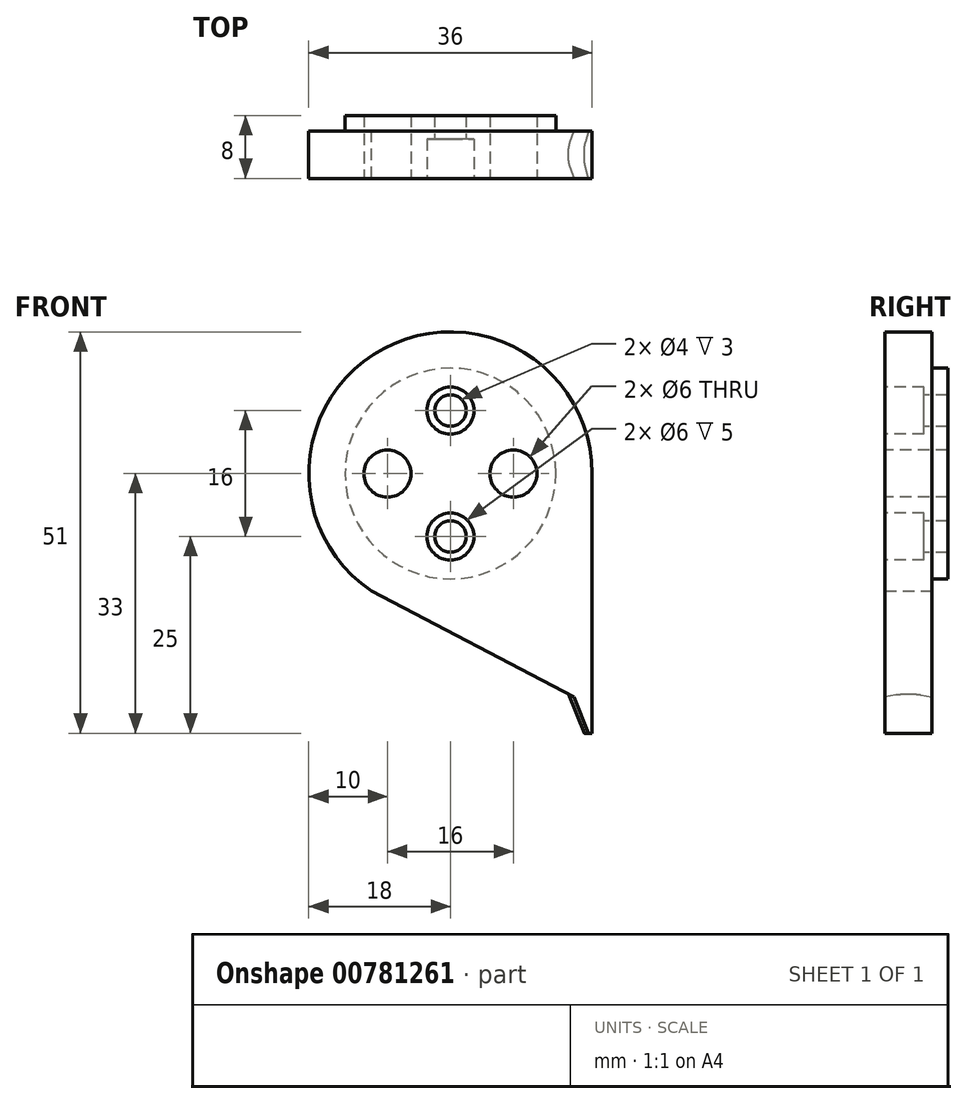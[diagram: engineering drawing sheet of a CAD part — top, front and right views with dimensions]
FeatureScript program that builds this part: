
annotation { "Feature Type Name" : "Feature", "Feature Type Description" : "" }
export const myFeature = defineFeature(function(context is Context, id is Id, definition is map)
    precondition{}
    {
        {
            var Q0;
            Q0=qCreatedBy(makeId("Front.planeOp"),FACE);
            var sketch = newSketch(context, id + "F0", { "sketchPlane" : qUnion([Q0])});
            skCircle(sketch, "E0", {"center": v(0, 0) * mm, "radius": 18 * mm});
            skLineSegment(sketch, "E1", {"start": v(18, 0) * mm, "end": v(18, -33) * mm});
            skLineSegment(sketch, "E2", {"start": v(18, -33) * mm, "end": v(15, -33) * mm});
            skLineSegment(sketch, "E3", {"start": v(15, -33) * mm, "end": v(15, -28) * mm});
            skLineSegment(sketch, "E4", {"start": v(15, -28) * mm, "end": v(-10.04, -14.94) * mm});
            skSolve(sketch);
        }
        {
            var Q0;
            {var subQ0=sQuery(id+"F0.wireOp",EDGE,"E0");var subQ1=makeQuery(id+"F0.imprint","INTERSECT",VERTEX,{"derivedFrom":[subQ0,sQuery(id+"F0.wireOp",EDGE,"E1")]});Q0=makeQuery(id+"F0.imprint","IMPRINT",FACE,{"disambiguationData":[TD([[makeQuery(id+"F0.imprint","IMPRINT",EDGE,{"disambiguationData":[TD([[subQ1,-1.0]])],"derivedFrom":subQ0}),1.0]])]});}
            var Q1;
            {var subQ1=sQuery(id+"F0.wireOp",EDGE,"E1");Q1=makeQuery(id+"F0.imprint","IMPRINT",FACE,{"disambiguationData":[TD([[makeQuery(id+"F0.imprint","IMPRINT",EDGE,{"derivedFrom":subQ1}),-1.0]])]});}
            extrude(context, id + "F1", {"entities" : qUnion([Q0, Q1]), "depth" : 6 * mm, "offsetDistance" : 25 * mm});
        }
        {
            var Q0;
            Q0=makeQuery(id+"F1.opExtrude","SWEPT_EDGE",EDGE,{"disambiguationData":[OSD([sQuery(id+"F0.wireOp",EDGE,"E2"),sQuery(id+"F0.wireOp",EDGE,"E3")])]});
            chamfer(context, id + "F2", {"entities" : qUnion([Q0]), "chamferType" : ChamferType.TWO_OFFSETS, "width1" : 2 * mm, "oppositeDirection" : false, "width2" : 5 * mm, "tangentPropagation" : true});
        }
        {
            var Q0;
            {var subQ0=sQuery(id+"F0.wireOp",EDGE,"E3");var subQ1=sQuery(id+"F0.wireOp",EDGE,"E2");Q0=makeQuery(id+"F2.opChamfer","BLEND_EDGE",EDGE,{"blendedFrom":[makeQuery(id+"F1.opExtrude","SWEPT_EDGE",EDGE,{"disambiguationData":[OSD([subQ1,subQ0])]}),makeQuery(id+"F1.opExtrude","CAP_FACE",FACE,{"disambiguationData":[OSD([sQuery(id+"F0.wireOp",EDGE,"E0"),sQuery(id+"F0.wireOp",EDGE,"E1"),subQ1,subQ0,sQuery(id+"F0.wireOp",EDGE,"E4")])],"isStart":true})],"blendedInto":[makeQuery(id+"F1.opExtrude","CAP_FACE",FACE,{"disambiguationData":[OSD([sQuery(id+"F0.wireOp",EDGE,"E0"),sQuery(id+"F0.wireOp",EDGE,"E1"),subQ1,subQ0,sQuery(id+"F0.wireOp",EDGE,"E4")])],"isStart":true})]});}
            var Q1;
            {var subQ0=sQuery(id+"F0.wireOp",EDGE,"E3");var subQ1=sQuery(id+"F0.wireOp",EDGE,"E2");Q1=makeQuery(id+"F2.opChamfer","BLEND_EDGE",EDGE,{"blendedFrom":[makeQuery(id+"F1.opExtrude","SWEPT_EDGE",EDGE,{"disambiguationData":[OSD([subQ1,subQ0])]}),makeQuery(id+"F1.opExtrude","CAP_FACE",FACE,{"disambiguationData":[OSD([sQuery(id+"F0.wireOp",EDGE,"E0"),sQuery(id+"F0.wireOp",EDGE,"E1"),subQ1,subQ0,sQuery(id+"F0.wireOp",EDGE,"E4")])],"isStart":false})],"blendedInto":[makeQuery(id+"F1.opExtrude","CAP_FACE",FACE,{"disambiguationData":[OSD([sQuery(id+"F0.wireOp",EDGE,"E0"),sQuery(id+"F0.wireOp",EDGE,"E1"),subQ1,subQ0,sQuery(id+"F0.wireOp",EDGE,"E4")])],"isStart":false})]});}
            chamfer(context, id + "F3", {"entities" : qUnion([Q0, Q1]), "chamferType" : ChamferType.TWO_OFFSETS, "width1" : .5 * mm, "oppositeDirection" : false, "width2" : 2 * mm, "tangentPropagation" : true});
        }
        {
            var Q0;
            {var subQ0=sQuery(id+"F0.wireOp",EDGE,"E3");var subQ1=sQuery(id+"F0.wireOp",EDGE,"E2");Q0=makeQuery(id+"F3.opChamfer","BLEND_EDGE",EDGE,{"blendedFrom":[makeQuery(id+"F2.opChamfer","BLEND_EDGE",EDGE,{"blendedFrom":[makeQuery(id+"F1.opExtrude","SWEPT_EDGE",EDGE,{"disambiguationData":[OSD([subQ1,subQ0])]}),makeQuery(id+"F1.opExtrude","CAP_FACE",FACE,{"disambiguationData":[OSD([sQuery(id+"F0.wireOp",EDGE,"E0"),sQuery(id+"F0.wireOp",EDGE,"E1"),subQ1,subQ0,sQuery(id+"F0.wireOp",EDGE,"E4")])],"isStart":true})],"blendedInto":[makeQuery(id+"F1.opExtrude","CAP_FACE",FACE,{"disambiguationData":[OSD([sQuery(id+"F0.wireOp",EDGE,"E0"),sQuery(id+"F0.wireOp",EDGE,"E1"),subQ1,subQ0,sQuery(id+"F0.wireOp",EDGE,"E4")])],"isStart":true})]}),makeQuery(id+"F2.opChamfer","BLEND_FACE",FACE,{"disambiguationData":[OSD([subQ1,subQ0])]})],"blendedInto":[makeQuery(id+"F2.opChamfer","BLEND_FACE",FACE,{"disambiguationData":[OSD([subQ1,subQ0])]})]});}
            var Q1;
            {var subQ0=sQuery(id+"F0.wireOp",EDGE,"E3");var subQ1=sQuery(id+"F0.wireOp",EDGE,"E2");Q1=makeQuery(id+"F3.opChamfer","BLEND_EDGE",EDGE,{"blendedFrom":[makeQuery(id+"F2.opChamfer","BLEND_EDGE",EDGE,{"blendedFrom":[makeQuery(id+"F1.opExtrude","SWEPT_EDGE",EDGE,{"disambiguationData":[OSD([subQ1,subQ0])]}),makeQuery(id+"F1.opExtrude","CAP_FACE",FACE,{"disambiguationData":[OSD([sQuery(id+"F0.wireOp",EDGE,"E0"),sQuery(id+"F0.wireOp",EDGE,"E1"),subQ1,subQ0,sQuery(id+"F0.wireOp",EDGE,"E4")])],"isStart":false})],"blendedInto":[makeQuery(id+"F1.opExtrude","CAP_FACE",FACE,{"disambiguationData":[OSD([sQuery(id+"F0.wireOp",EDGE,"E0"),sQuery(id+"F0.wireOp",EDGE,"E1"),subQ1,subQ0,sQuery(id+"F0.wireOp",EDGE,"E4")])],"isStart":false})]}),makeQuery(id+"F2.opChamfer","BLEND_FACE",FACE,{"disambiguationData":[OSD([subQ1,subQ0])]})],"blendedInto":[makeQuery(id+"F2.opChamfer","BLEND_FACE",FACE,{"disambiguationData":[OSD([subQ1,subQ0])]})]});}
            fillet(context, id + "F4", {"entities" : qUnion([Q0, Q1]), "radius" : 5 * mm, "tangentPropagation" : true, "allowEdgeOverflow" : false});
        }
        {
            var Q0;
            Q0=makeQuery(id+"F1.opExtrude","CAP_FACE",FACE,{"disambiguationData":[OSD([sQuery(id+"F0.wireOp",EDGE,"E0"),sQuery(id+"F0.wireOp",EDGE,"E1"),sQuery(id+"F0.wireOp",EDGE,"E2"),sQuery(id+"F0.wireOp",EDGE,"E3"),sQuery(id+"F0.wireOp",EDGE,"E4")])],"isStart":false});
            var sketch = newSketch(context, id + "F5", { "sketchPlane" : qUnion([Q0])});
            skCircle(sketch, "E5", {"center": v(0, 8) * mm, "radius": 2 * mm});
            skCircle(sketch, "E6", {"center": v(0, -8) * mm, "radius": 2 * mm});
            skCircle(sketch, "E7", {"center": v(8, 0) * mm, "radius": 3 * mm});
            skCircle(sketch, "E8", {"center": v(-8, 0) * mm, "radius": 3 * mm});
            skCircle(sketch, "E9", {"center": v(0, 0) * mm, "radius": 13.38 * mm});
            skCircle(sketch, "E10", {"center": v(0, 8) * mm, "radius": 3 * mm});
            skCircle(sketch, "E11", {"center": v(0, -8) * mm, "radius": 3 * mm});
            skSolve(sketch);
        }
        {
            var Q0;
            Q0=makeQuery(id+"F5.imprint","IMPRINT",FACE,{"disambiguationData":[TD([[makeQuery(id+"F5.imprint","IMPRINT",EDGE,{"derivedFrom":sQuery(id+"F5.wireOp",EDGE,"E5")}),-1.0]])]});
            var Q1;
            Q1=makeQuery(id+"F5.imprint","IMPRINT",FACE,{"disambiguationData":[TD([[makeQuery(id+"F5.imprint","IMPRINT",EDGE,{"derivedFrom":sQuery(id+"F5.wireOp",EDGE,"E8")}),1.0]])]});
            var Q2;
            Q2=makeQuery(id+"F5.imprint","IMPRINT",FACE,{"disambiguationData":[TD([[makeQuery(id+"F5.imprint","IMPRINT",EDGE,{"derivedFrom":sQuery(id+"F5.wireOp",EDGE,"E5")}),1.0]])]});
            var Q3;
            Q3=makeQuery(id+"F5.imprint","IMPRINT",FACE,{"disambiguationData":[TD([[makeQuery(id+"F5.imprint","IMPRINT",EDGE,{"derivedFrom":sQuery(id+"F5.wireOp",EDGE,"E7")}),1.0]])]});
            var Q4;
            Q4=makeQuery(id+"F5.imprint","IMPRINT",FACE,{"disambiguationData":[TD([[makeQuery(id+"F5.imprint","IMPRINT",EDGE,{"derivedFrom":sQuery(id+"F5.wireOp",EDGE,"E6")}),1.0]])]});
            var Q5;
            Q5=makeQuery(id+"F5.imprint","IMPRINT",FACE,{"disambiguationData":[TD([[makeQuery(id+"F5.imprint","IMPRINT",EDGE,{"derivedFrom":sQuery(id+"F5.wireOp",EDGE,"E7")}),-1.0]])]});
            var Q6;
            Q6=makeQuery(id+"F5.imprint","IMPRINT",FACE,{"disambiguationData":[TD([[makeQuery(id+"F5.imprint","IMPRINT",EDGE,{"derivedFrom":sQuery(id+"F5.wireOp",EDGE,"E6")}),-1.0]])]});
            extrude(context, id + "F6", {"entities" : qUnion([Q0, Q1, Q2, Q3, Q4, Q5, Q6]), "operationType" : NewBodyOperationType.ADD, "oppositeDirection" : true, "depth" : 8 * mm, "offsetDistance" : 25 * mm});
        }
        {
            var Q0;
            Q0=makeQuery(id+"F5.imprint","IMPRINT",FACE,{"disambiguationData":[TD([[makeQuery(id+"F5.imprint","IMPRINT",EDGE,{"derivedFrom":sQuery(id+"F5.wireOp",EDGE,"E8")}),1.0]])]});
            var Q1;
            Q1=makeQuery(id+"F5.imprint","IMPRINT",FACE,{"disambiguationData":[TD([[makeQuery(id+"F5.imprint","IMPRINT",EDGE,{"derivedFrom":sQuery(id+"F5.wireOp",EDGE,"E5")}),1.0]])]});
            var Q2;
            Q2=makeQuery(id+"F5.imprint","IMPRINT",FACE,{"disambiguationData":[TD([[makeQuery(id+"F5.imprint","IMPRINT",EDGE,{"derivedFrom":sQuery(id+"F5.wireOp",EDGE,"E7")}),1.0]])]});
            var Q3;
            Q3=makeQuery(id+"F5.imprint","IMPRINT",FACE,{"disambiguationData":[TD([[makeQuery(id+"F5.imprint","IMPRINT",EDGE,{"derivedFrom":sQuery(id+"F5.wireOp",EDGE,"E6")}),1.0]])]});
            extrude(context, id + "F7", {"entities" : qUnion([Q0, Q1, Q2, Q3]), "operationType" : NewBodyOperationType.REMOVE, "endBound" : BoundingType.THROUGH_ALL, "oppositeDirection" : true, "depth" : 25 * mm, "offsetDistance" : 25 * mm});
        }
        {
            var Q0;
            Q0=makeQuery(id+"F5.imprint","IMPRINT",FACE,{"disambiguationData":[TD([[makeQuery(id+"F5.imprint","IMPRINT",EDGE,{"derivedFrom":sQuery(id+"F5.wireOp",EDGE,"E5")}),-1.0]])]});
            var Q1;
            Q1=makeQuery(id+"F5.imprint","IMPRINT",FACE,{"disambiguationData":[TD([[makeQuery(id+"F5.imprint","IMPRINT",EDGE,{"derivedFrom":sQuery(id+"F5.wireOp",EDGE,"E6")}),-1.0]])]});
            extrude(context, id + "F8", {"entities" : qUnion([Q0, Q1]), "operationType" : NewBodyOperationType.REMOVE, "oppositeDirection" : true, "depth" : 5 * mm, "offsetDistance" : 25 * mm});
        }
    });
